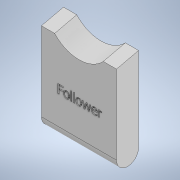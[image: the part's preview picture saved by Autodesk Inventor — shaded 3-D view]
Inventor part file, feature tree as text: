
AUTODESK INVENTOR PART (.ipt)
format: ipt  version: 2021 (Build 250183000, 183)  size: 259,072 bytes
history: native  units: mm
features: sketch x5, extrude x2, fillet x1, plane x1, sweep x1, emboss x1
ambient origin geometry x8: Origin, YZ Plane, XZ Plane, XY Plane, X Axis, Y Axis, Z Axis, Center Point
bodies: Solid1 (feature_tree)
feature tree (11):
  extrude  "Extrusion1"  Depth=21.5mm
  fillet  "Fillet2"  Radius=5.0mm
  plane  "Work Plane1"
  sweep  "Sweep1"
  extrude  "Extrusion6"  TaperAngle=0.0deg  [1 undecoded]
  emboss  "Emboss1"
  sketch  "Sketch1"  dims[d0=17.0mm d1=21.5mm d2=5.0mm d3=0.0mm]
  sketch  "Sketch5"  dims[d15=2.5mm d21=-8.5mm]
  sketch  "Sketch6"  dims[d22=2.268928mm d25=0.0mm d26=0.0mm]
  sketch  "Sketch8"  dims[d27=3.0mm]
  sketch  "Sketch9"  dims[d31=3.0mm d32=3.0mm d33=3.0mm d34=7.5mm d35=17.0mm d36=0.0mm d37=1.0mm d38=0.0mm d16=0.872665mm d17=0.5mm d18=0.872665mm]
note: 1 required parameter value undecoded (feature->parameter linkage not recoverable at this tier; creation-order binding heuristic only, values carry confidence <= 0.55)
